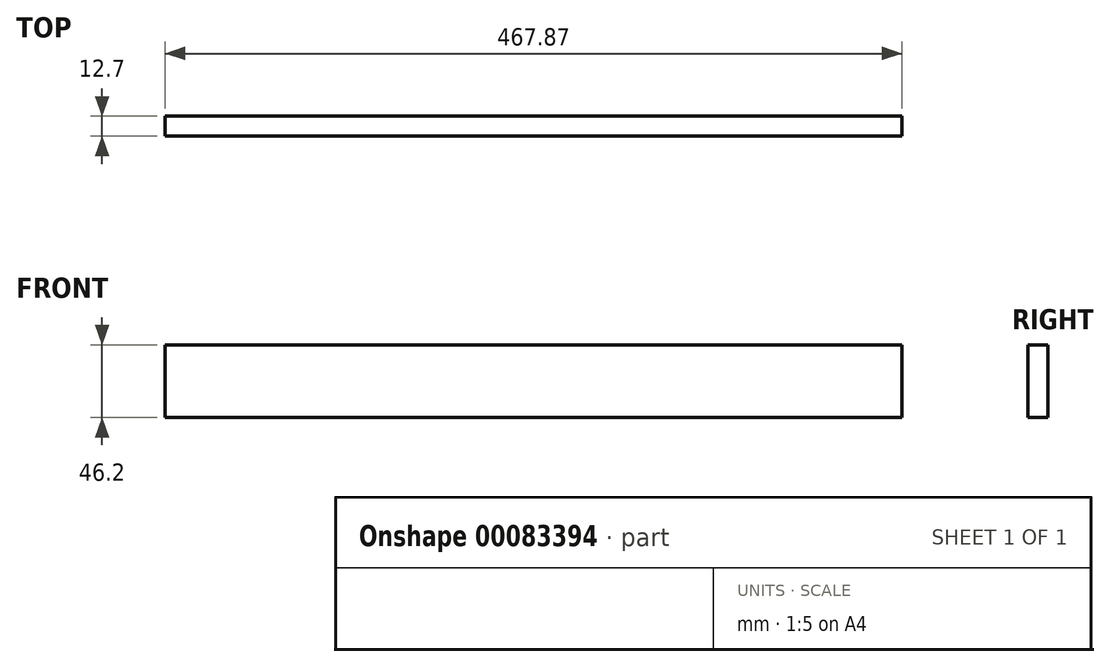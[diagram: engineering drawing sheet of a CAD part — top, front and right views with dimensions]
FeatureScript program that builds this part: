
annotation { "Feature Type Name" : "Feature", "Feature Type Description" : "" }
export const myFeature = defineFeature(function(context is Context, id is Id, definition is map)
    precondition{}
    {
        {
            var Q0;
            Q0=qCreatedBy(makeId("Front.planeOp"),FACE);
            var sketch = newSketch(context, id + "F0", { "sketchPlane" : qUnion([Q0])});
            skLineSegment(sketch, "E0.bottom", {"start": v(185.53, -58.3) * mm, "end": v(-282.34, -58.3) * mm});
            skLineSegment(sketch, "E0.top", {"start": v(185.53, -12.1) * mm, "end": v(-282.34, -12.1) * mm});
            skLineSegment(sketch, "E0.left", {"start": v(185.53, -58.3) * mm, "end": v(185.53, -12.1) * mm});
            skLineSegment(sketch, "E0.right", {"start": v(-282.34, -58.3) * mm, "end": v(-282.34, -12.1) * mm});
            skSolve(sketch);
        }
        {
            var Q0;
            Q0 = qSketchRegion(id + "F0", true);
            extrude(context, id + "F1", {"entities" : qUnion([Q0]), "depth" : 12.7 * mm});
        }
    });
